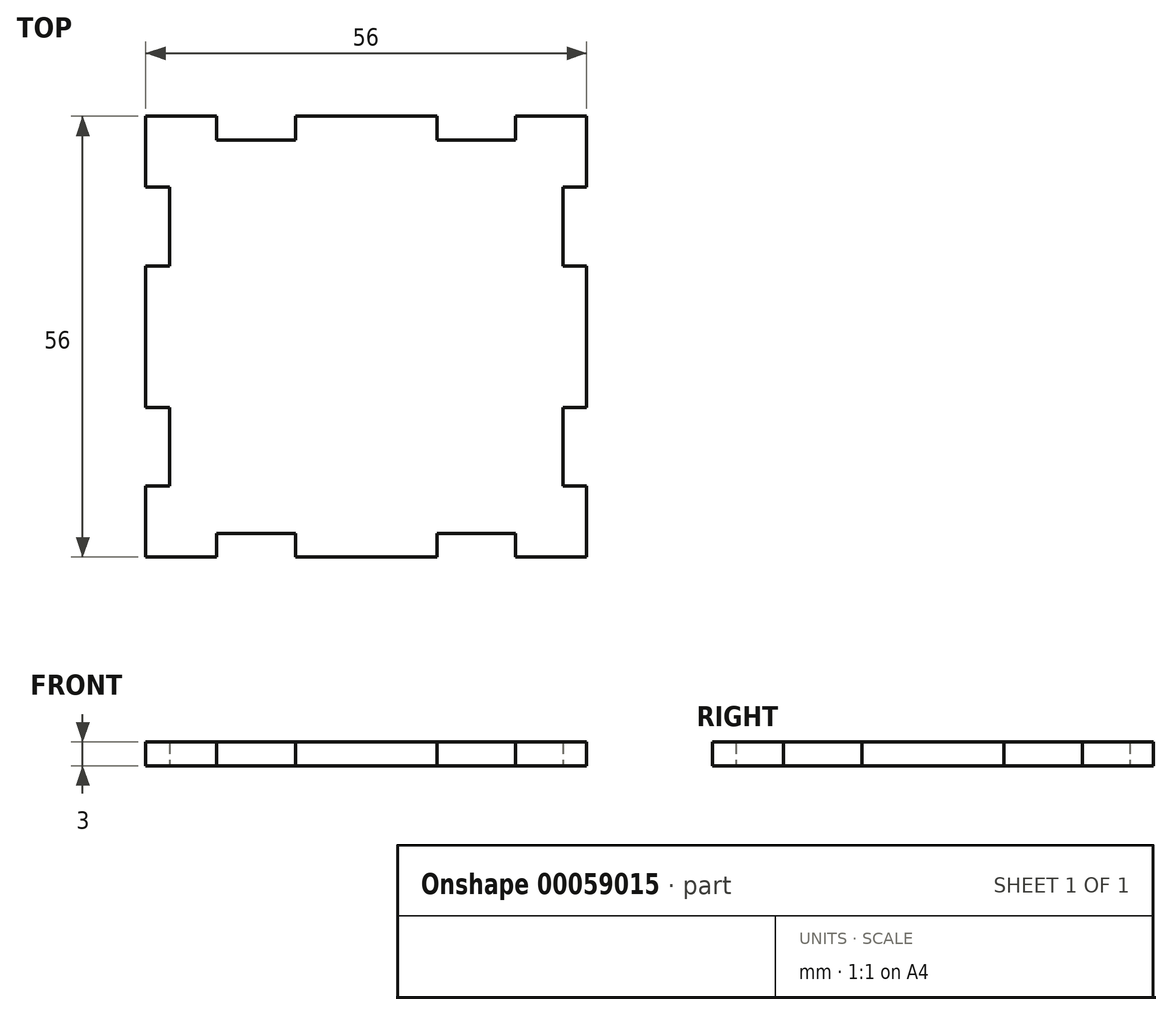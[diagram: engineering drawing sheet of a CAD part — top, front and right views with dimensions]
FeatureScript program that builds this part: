
annotation { "Feature Type Name" : "Feature", "Feature Type Description" : "" }
export const myFeature = defineFeature(function(context is Context, id is Id, definition is map)
    precondition{}
    {
        {
            var Q0;
            Q0=qCreatedBy(makeId("Top.planeOp"),FACE);
            var sketch = newSketch(context, id + "F0", { "sketchPlane" : qUnion([Q0])});
            skLineSegment(sketch, "E0.rect.bottom", {"start": v(-28, 28) * mm, "end": v(-19, 28) * mm});
            skLineSegment(sketch, "E0.rect.top", {"start": v(-28, -28) * mm, "end": v(-19, -28) * mm});
            skLineSegment(sketch, "E0.rect.left", {"start": v(-28, 28) * mm, "end": v(-28, 19) * mm});
            skLineSegment(sketch, "E0.rect.right", {"start": v(28, 28) * mm, "end": v(28, 19) * mm});
            skPoint(sketch, "E0.rect.middle", {"position": v(0, 0) * mm});
            skLineSegment(sketch, "E1.top", {"start": v(-19, 25) * mm, "end": v(-9, 25) * mm});
            skLineSegment(sketch, "E1.left", {"start": v(-19, 28) * mm, "end": v(-19, 25) * mm});
            skLineSegment(sketch, "E1.right", {"start": v(-9, 28) * mm, "end": v(-9, 25) * mm});
            skLineSegment(sketch, "E2.trimOffspring", {"start": v(-9, 28) * mm, "end": v(9, 28) * mm});
            skLineSegment(sketch, "E3.MirrorCS", {"start": v(19, 25) * mm, "end": v(9, 25) * mm});
            skLineSegment(sketch, "E4.MirrorCS", {"start": v(19, 28) * mm, "end": v(19, 25) * mm});
            skLineSegment(sketch, "E5.MirrorCS", {"start": v(9, 28) * mm, "end": v(9, 25) * mm});
            skLineSegment(sketch, "E6.MirrorCS", {"start": v(-19, -28) * mm, "end": v(-19, -25) * mm});
            skLineSegment(sketch, "E7.MirrorCS", {"start": v(-19, -25) * mm, "end": v(-9, -25) * mm});
            skLineSegment(sketch, "E8.MirrorCS", {"start": v(-9, -28) * mm, "end": v(-9, -25) * mm});
            skLineSegment(sketch, "E9.MirrorCS", {"start": v(9, -28) * mm, "end": v(9, -25) * mm});
            skLineSegment(sketch, "E10.MirrorCS", {"start": v(19, -28) * mm, "end": v(19, -25) * mm});
            skLineSegment(sketch, "E11.MirrorCS", {"start": v(19, -25) * mm, "end": v(9, -25) * mm});
            skLineSegment(sketch, "E12.trimOffspring", {"start": v(-9, -28) * mm, "end": v(9, -28) * mm});
            skLineSegment(sketch, "E13.trimOffspring", {"start": v(19, -28) * mm, "end": v(28, -28) * mm});
            skLineSegment(sketch, "E14.trimOffspring", {"start": v(19, 28) * mm, "end": v(28, 28) * mm});
            skLineSegment(sketch, "E15.bottom", {"start": v(-28, 19) * mm, "end": v(-25, 19) * mm});
            skLineSegment(sketch, "E15.top", {"start": v(-28, 9) * mm, "end": v(-25, 9) * mm});
            skLineSegment(sketch, "E15.right", {"start": v(-25, 19) * mm, "end": v(-25, 9) * mm});
            skLineSegment(sketch, "E16.trimOffspring", {"start": v(-28, 9) * mm, "end": v(-28, -9) * mm});
            skLineSegment(sketch, "E17.MirrorCS", {"start": v(-25, -19) * mm, "end": v(-25, -9) * mm});
            skLineSegment(sketch, "E18.MirrorCS", {"start": v(-28, -19) * mm, "end": v(-25, -19) * mm});
            skLineSegment(sketch, "E19.MirrorCS", {"start": v(-28, -9) * mm, "end": v(-25, -9) * mm});
            skLineSegment(sketch, "E20.trimOffspring", {"start": v(-28, -19) * mm, "end": v(-28, -28) * mm});
            skLineSegment(sketch, "E21.MirrorCS", {"start": v(28, -19) * mm, "end": v(25, -19) * mm});
            skLineSegment(sketch, "E22.MirrorCS", {"start": v(25, -19) * mm, "end": v(25, -9) * mm});
            skLineSegment(sketch, "E23.MirrorCS", {"start": v(28, -9) * mm, "end": v(25, -9) * mm});
            skLineSegment(sketch, "E24.MirrorCS", {"start": v(28, 9) * mm, "end": v(25, 9) * mm});
            skLineSegment(sketch, "E25.MirrorCS", {"start": v(28, 19) * mm, "end": v(25, 19) * mm});
            skLineSegment(sketch, "E26.MirrorCS", {"start": v(25, 19) * mm, "end": v(25, 9) * mm});
            skLineSegment(sketch, "E27.trimOffspring", {"start": v(28, 9) * mm, "end": v(28, -9) * mm});
            skLineSegment(sketch, "E28.trimOffspring", {"start": v(28, -19) * mm, "end": v(28, -28) * mm});
            skSolve(sketch);
        }
        {
            var Q0;
            Q0 = qSketchRegion(id + "F0", true);
            extrude(context, id + "F1", {"entities" : qUnion([Q0]), "depth" : 3 * mm});
        }
    });
